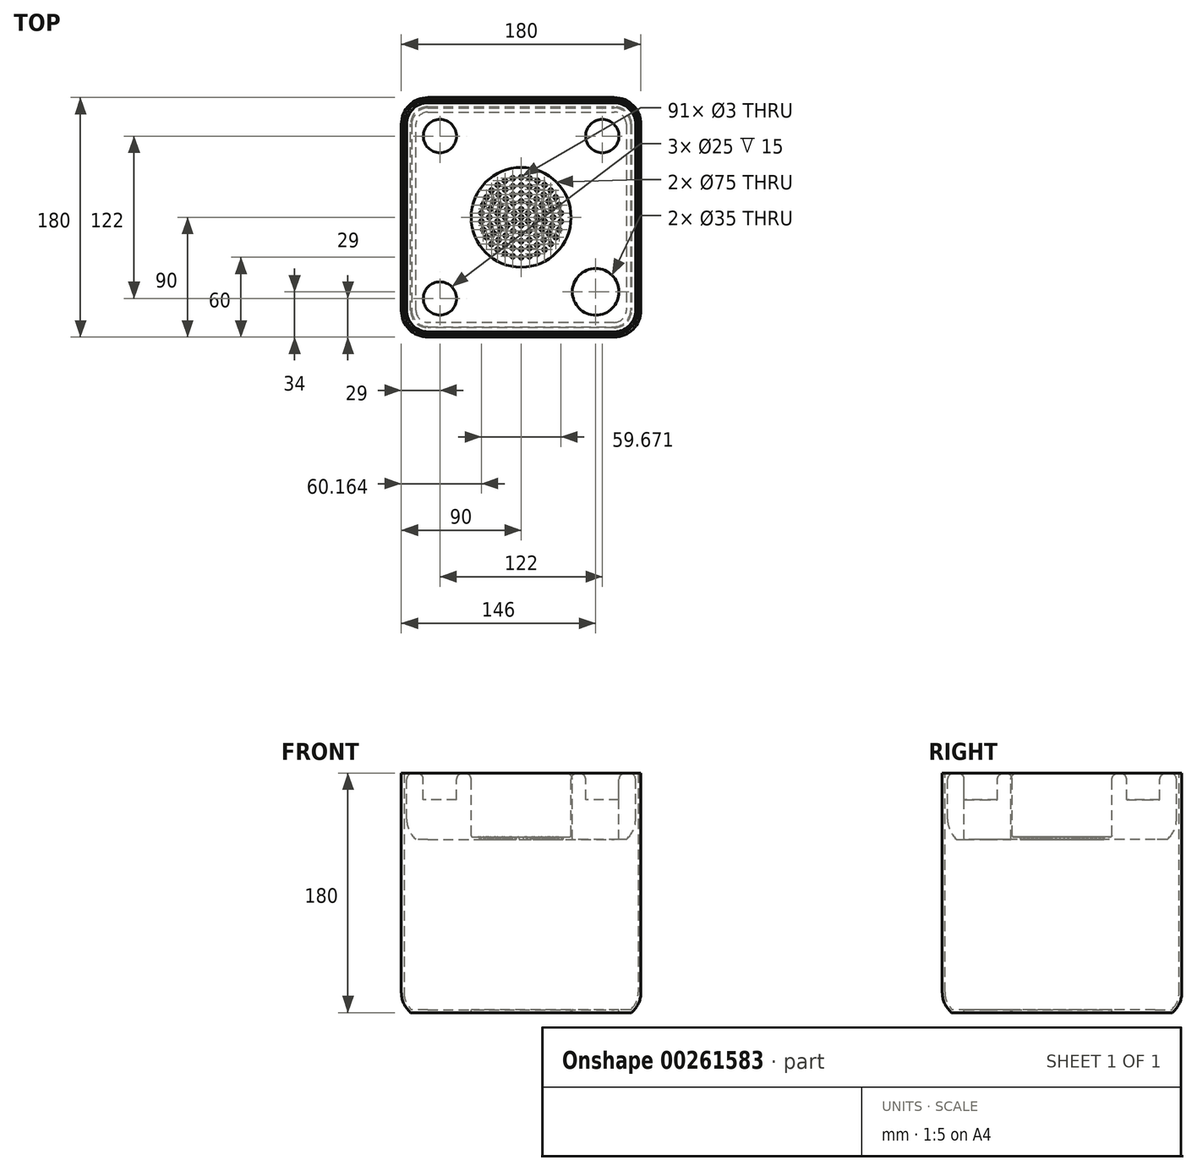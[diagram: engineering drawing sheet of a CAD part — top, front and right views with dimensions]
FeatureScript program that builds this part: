
annotation { "Feature Type Name" : "Feature", "Feature Type Description" : "" }
export const myFeature = defineFeature(function(context is Context, id is Id, definition is map)
    precondition{}
    {
        {
            var Q0;
            Q0=qCreatedBy(makeId("Top.planeOp"),FACE);
            var sketch = newSketch(context, id + "F0", { "sketchPlane" : qUnion([Q0])});
            skLineSegment(sketch, "E0.bottom", {"start": v(-90, 90) * mm, "end": v(90, 90) * mm});
            skLineSegment(sketch, "E0.top", {"start": v(-90, -90) * mm, "end": v(90, -90) * mm});
            skLineSegment(sketch, "E0.left", {"start": v(-90, 90) * mm, "end": v(-90, -90) * mm});
            skLineSegment(sketch, "E0.right", {"start": v(90, 90) * mm, "end": v(90, -90) * mm});
            skPoint(sketch, "E0.middle", {"position": v(0, 0) * mm});
            skSolve(sketch);
        }
        {
            var Q0;
            Q0 = qSketchRegion(id + "F0", true);
            extrude(context, id + "F1", {"entities" : qUnion([Q0]), "depth" : 180 * mm});
        }
        {
            var Q0;
            Q0=makeQuery(id+"F1.opExtrude","SWEPT_EDGE",EDGE,{"disambiguationData":[OSD([sQuery(id+"F0.wireOp",EDGE,"E0.top"),sQuery(id+"F0.wireOp",EDGE,"E0.right")])]});
            var Q1;
            Q1=makeQuery(id+"F1.opExtrude","SWEPT_EDGE",EDGE,{"disambiguationData":[OSD([sQuery(id+"F0.wireOp",EDGE,"E0.top"),sQuery(id+"F0.wireOp",EDGE,"E0.left")])]});
            var Q2;
            Q2=makeQuery(id+"F1.opExtrude","SWEPT_EDGE",EDGE,{"disambiguationData":[OSD([sQuery(id+"F0.wireOp",EDGE,"E0.bottom"),sQuery(id+"F0.wireOp",EDGE,"E0.right")])]});
            var Q3;
            Q3=makeQuery(id+"F1.opExtrude","SWEPT_EDGE",EDGE,{"disambiguationData":[OSD([sQuery(id+"F0.wireOp",EDGE,"E0.bottom"),sQuery(id+"F0.wireOp",EDGE,"E0.left")])]});
            fillet(context, id + "F2", {"entities" : qUnion([Q0, Q1, Q2, Q3]), "radius" : 20 * mm, "tangentPropagation" : true, "allowEdgeOverflow" : false});
        }
        {
            var Q0;
            Q0=makeQuery(id+"F1.opExtrude","CAP_FACE",FACE,{"disambiguationData":[OSD([sQuery(id+"F0.wireOp",EDGE,"E0.bottom"),sQuery(id+"F0.wireOp",EDGE,"E0.top"),sQuery(id+"F0.wireOp",EDGE,"E0.left"),sQuery(id+"F0.wireOp",EDGE,"E0.right")])],"isStart":true});
            chamfer(context, id + "F3", {"entities" : qUnion([Q0]), "width" : 7 * mm, "tangentPropagation" : true});
        }
        {
            var Q0;
            {var subQ0=sQuery(id+"F0.wireOp",EDGE,"E0.left");Q0=makeQuery(id+"F3.opChamfer","BLEND_EDGE",EDGE,{"blendedFrom":[makeQuery(id+"F1.opExtrude","CAP_EDGE",EDGE,{"disambiguationData":[OSD([subQ0])],"isStart":true}),makeQuery(id+"F1.opExtrude","SWEPT_FACE",FACE,{"disambiguationData":[OSD([subQ0])]})],"blendedInto":[makeQuery(id+"F1.opExtrude","SWEPT_FACE",FACE,{"disambiguationData":[OSD([subQ0])]})]});}
            fillet(context, id + "F4", {"entities" : qUnion([Q0]), "radius" : 20 * mm, "tangentPropagation" : true, "allowEdgeOverflow" : false});
        }
        {
            var Q0;
            Q0=makeQuery(id+"F1.opExtrude","CAP_FACE",FACE,{"disambiguationData":[OSD([sQuery(id+"F0.wireOp",EDGE,"E0.bottom"),sQuery(id+"F0.wireOp",EDGE,"E0.top"),sQuery(id+"F0.wireOp",EDGE,"E0.left"),sQuery(id+"F0.wireOp",EDGE,"E0.right")])],"isStart":false});
            shell(context, id + "F5", {"entities" : qUnion([Q0]), "thickness" : 2 * mm});
        }
        {
            var Q0;
            Q0=makeQuery(id+"F4YuCpgrHovAHZC_1.boolean.opBoolean","MERGE",FACE,{"derivedFrom":[makeQuery(id+"F1.opExtrude","CAP_FACE",FACE,{"disambiguationData":[OSD([sQuery(id+"F0.wireOp",EDGE,"E0.bottom"),sQuery(id+"F0.wireOp",EDGE,"E0.top"),sQuery(id+"F0.wireOp",EDGE,"E0.left"),sQuery(id+"F0.wireOp",EDGE,"E0.right")])],"isStart":false}),makeQuery(id+"F4YuCpgrHovAHZC_1.opExtrude","CAP_FACE",FACE,{"disambiguationData":[OSD([sQuery(id+"F18IyqBRE7dcMwR_1.wireOp",EDGE,"iNaZnhlK-WJTm-0Kn5-Of0J-zMqdmAbUonz0.top"),sQuery(id+"F18IyqBRE7dcMwR_1.wireOp",EDGE,"iNaZnhlK-WJTm-0Kn5-Of0J-zMqdmAbUonz0.left"),sQuery(id+"F18IyqBRE7dcMwR_1.wireOp",EDGE,"z2CsC4pT-1LaP-1Rqi-iMAI-N6OsgD8oTBJP"),sQuery(id+"F18IyqBRE7dcMwR_1.wireOp",EDGE,"xvhJzDiT-tZiE-QDcA-WI1C-gXQeY3Zw0ukX"),sQuery(id+"F18IyqBRE7dcMwR_1.wireOp",EDGE,"OlVmHNYn-kKTD-olFf-enFW-YJtCeyeuMl2Y")])],"isStart":true})]});
            var sketch = newSketch(context, id + "F6", { "sketchPlane" : qUnion([Q0])});
            skArc(sketch, "E1.0", {"start": v(-70, 88) * mm, "mid": v(-82.73, 82.73) * mm, "end": v(-88, 70) * mm, "construction": true});
            skLineSegment(sketch, "E1.1", {"start": v(-70, 88) * mm, "end": v(70, 88) * mm, "construction": true});
            skArc(sketch, "E1.2", {"start": v(88, 70) * mm, "mid": v(82.73, 82.73) * mm, "end": v(70, 88) * mm, "construction": true});
            skLineSegment(sketch, "E1.3", {"start": v(88, 70) * mm, "end": v(88, -70) * mm, "construction": true});
            skArc(sketch, "E1.4", {"start": v(70, -88) * mm, "mid": v(82.73, -82.73) * mm, "end": v(88, -70) * mm, "construction": true});
            skLineSegment(sketch, "E1.5", {"start": v(-70, -88) * mm, "end": v(70, -88) * mm, "construction": true});
            skArc(sketch, "E1.6", {"start": v(-88, -70) * mm, "mid": v(-82.73, -82.73) * mm, "end": v(-70, -88) * mm, "construction": true});
            skLineSegment(sketch, "E1.7", {"start": v(-88, 70) * mm, "end": v(-88, -70) * mm, "construction": true});
            skLineSegment(sketch, "E2.0", {"start": v(-70, -86) * mm, "end": v(70, -86) * mm});
            skArc(sketch, "E2.1", {"start": v(-86, -70) * mm, "mid": v(-81.31, -81.31) * mm, "end": v(-70, -86) * mm});
            skArc(sketch, "E2.2", {"start": v(70, -86) * mm, "mid": v(81.31, -81.31) * mm, "end": v(86, -70) * mm});
            skLineSegment(sketch, "E2.3", {"start": v(-86, 70) * mm, "end": v(-86, -70) * mm});
            skLineSegment(sketch, "E2.4", {"start": v(86, 70) * mm, "end": v(86, -70) * mm});
            skArc(sketch, "E2.5", {"start": v(86, 70) * mm, "mid": v(81.31, 81.31) * mm, "end": v(70, 86) * mm});
            skLineSegment(sketch, "E2.6", {"start": v(-70, 86) * mm, "end": v(70, 86) * mm});
            skArc(sketch, "E2.7", {"start": v(-70, 86) * mm, "mid": v(-81.31, 81.31) * mm, "end": v(-86, 70) * mm});
            skSolve(sketch);
        }
        {
            var Q0;
            Q0 = qSketchRegion(id + "F6", true);
            extrude(context, id + "F7", {"entities" : qUnion([Q0]), "oppositeDirection" : true, "depth" : 50 * mm});
        }
        {
            var Q0;
            Q0=makeQuery(id+"F7.opExtrude","CAP_FACE",FACE,{"disambiguationData":[OSD([sQuery(id+"F6.wireOp",EDGE,"E2.7"),sQuery(id+"F6.wireOp",EDGE,"E2.3"),sQuery(id+"F6.wireOp",EDGE,"E2.6"),sQuery(id+"F6.wireOp",EDGE,"E2.1"),sQuery(id+"F6.wireOp",EDGE,"E2.5"),sQuery(id+"F6.wireOp",EDGE,"E2.4"),sQuery(id+"F6.wireOp",EDGE,"E2.2"),sQuery(id+"F6.wireOp",EDGE,"E2.0")])],"isStart":true});
            var sketch = newSketch(context, id + "F8", { "sketchPlane" : qUnion([Q0])});
            skCircle(sketch, "E3", {"center": v(0, 0) * mm, "radius": 37.5 * mm});
            skSolve(sketch);
        }
        {
            var Q0;
            Q0=makeQuery(id+"F8.imprint","IMPRINT",FACE,{"disambiguationData":[TD([[makeQuery(id+"F8.imprint","IMPRINT",EDGE,{"derivedFrom":sQuery(id+"F8.wireOp",EDGE,"E3")}),1.0]])]});
            extrude(context, id + "F9", {"entities" : qUnion([Q0]), "operationType" : NewBodyOperationType.REMOVE, "endBound" : BoundingType.THROUGH_ALL, "oppositeDirection" : true, "depth" : 2 * mm});
        }
        {
            var Q0;
            Q0=makeQuery(id+"F7.opExtrude","CAP_FACE",FACE,{"disambiguationData":[OSD([sQuery(id+"F6.wireOp",EDGE,"E2.7"),sQuery(id+"F6.wireOp",EDGE,"E2.3"),sQuery(id+"F6.wireOp",EDGE,"E2.6"),sQuery(id+"F6.wireOp",EDGE,"E2.1"),sQuery(id+"F6.wireOp",EDGE,"E2.5"),sQuery(id+"F6.wireOp",EDGE,"E2.4"),sQuery(id+"F6.wireOp",EDGE,"E2.2"),sQuery(id+"F6.wireOp",EDGE,"E2.0")])],"isStart":false});
            var sketch = newSketch(context, id + "F10", { "sketchPlane" : qUnion([Q0])});
            skCircle(sketch, "E4.0", {"center": v(0, 0) * mm, "radius": 37.5 * mm});
            skCircle(sketch, "E5", {"center": v(0, 0) * mm, "radius": 6 * mm, "construction": true});
            skCircle(sketch, "E6", {"center": v(0, 0) * mm, "radius": 12 * mm, "construction": true});
            skCircle(sketch, "E7", {"center": v(0, 0) * mm, "radius": 18 * mm, "construction": true});
            skCircle(sketch, "E8", {"center": v(0, 0) * mm, "radius": 24 * mm, "construction": true});
            skCircle(sketch, "E9", {"center": v(0, 0) * mm, "radius": 30 * mm, "construction": true});
            skCircle(sketch, "E10", {"center": v(0, 0) * mm, "radius": 1.5 * mm});
            skCircle(sketch, "E11", {"center": v(0, 6) * mm, "radius": 1.5 * mm});
            skCircle(sketch, "E12", {"center": v(0, 12) * mm, "radius": 1.5 * mm});
            skCircle(sketch, "E13", {"center": v(0, 18) * mm, "radius": 1.5 * mm});
            skCircle(sketch, "E14", {"center": v(0, 24) * mm, "radius": 1.5 * mm});
            skCircle(sketch, "E15", {"center": v(0, 30) * mm, "radius": 1.5 * mm});
            skCircle(sketch, "E16.1.0", {"center": v(-5.2, 3) * mm, "radius": 1.5 * mm});
            skCircle(sketch, "E16.2.0", {"center": v(-5.2, -3) * mm, "radius": 1.5 * mm});
            skCircle(sketch, "E16.3.0", {"center": v(0, -6) * mm, "radius": 1.5 * mm});
            skCircle(sketch, "E16.4.0", {"center": v(5.2, -3) * mm, "radius": 1.5 * mm});
            skCircle(sketch, "E16.5.0", {"center": v(5.2, 3) * mm, "radius": 1.5 * mm});
            skCircle(sketch, "E17.1.0", {"center": v(-6, 10.4) * mm, "radius": 1.5 * mm});
            skCircle(sketch, "E17.2.0", {"center": v(-10.4, 6) * mm, "radius": 1.5 * mm});
            skCircle(sketch, "E17.3.0", {"center": v(-12, 0) * mm, "radius": 1.5 * mm});
            skCircle(sketch, "E17.4.0", {"center": v(-10.4, -6) * mm, "radius": 1.5 * mm});
            skCircle(sketch, "E17.5.0", {"center": v(-6, -10.4) * mm, "radius": 1.5 * mm});
            skCircle(sketch, "E17.6.0", {"center": v(0, -12) * mm, "radius": 1.5 * mm});
            skCircle(sketch, "E17.7.0", {"center": v(6, -10.4) * mm, "radius": 1.5 * mm});
            skCircle(sketch, "E17.8.0", {"center": v(10.4, -6) * mm, "radius": 1.5 * mm});
            skCircle(sketch, "E17.9.0", {"center": v(12, 0) * mm, "radius": 1.5 * mm});
            skCircle(sketch, "E17.10.0", {"center": v(10.4, 6) * mm, "radius": 1.5 * mm});
            skCircle(sketch, "E17.11.0", {"center": v(6, 10.4) * mm, "radius": 1.5 * mm});
            skCircle(sketch, "E18.1.0", {"center": v(-6.16, 16.91) * mm, "radius": 1.5 * mm});
            skCircle(sketch, "E18.2.0", {"center": v(-11.57, 13.79) * mm, "radius": 1.5 * mm});
            skCircle(sketch, "E18.3.0", {"center": v(-15.59, 9) * mm, "radius": 1.5 * mm});
            skCircle(sketch, "E18.4.0", {"center": v(-17.73, 3.13) * mm, "radius": 1.5 * mm});
            skCircle(sketch, "E18.5.0", {"center": v(-17.73, -3.13) * mm, "radius": 1.5 * mm});
            skCircle(sketch, "E18.6.0", {"center": v(-15.59, -9) * mm, "radius": 1.5 * mm});
            skCircle(sketch, "E18.7.0", {"center": v(-11.57, -13.79) * mm, "radius": 1.5 * mm});
            skCircle(sketch, "E18.8.0", {"center": v(-6.16, -16.91) * mm, "radius": 1.5 * mm});
            skCircle(sketch, "E18.9.0", {"center": v(0, -18) * mm, "radius": 1.5 * mm});
            skCircle(sketch, "E18.10.0", {"center": v(6.16, -16.91) * mm, "radius": 1.5 * mm});
            skCircle(sketch, "E18.11.0", {"center": v(11.57, -13.79) * mm, "radius": 1.5 * mm});
            skCircle(sketch, "E18.12.0", {"center": v(15.59, -9) * mm, "radius": 1.5 * mm});
            skCircle(sketch, "E18.13.0", {"center": v(17.73, -3.13) * mm, "radius": 1.5 * mm});
            skCircle(sketch, "E18.14.0", {"center": v(17.73, 3.13) * mm, "radius": 1.5 * mm});
            skCircle(sketch, "E18.15.0", {"center": v(15.59, 9) * mm, "radius": 1.5 * mm});
            skCircle(sketch, "E18.16.0", {"center": v(11.57, 13.79) * mm, "radius": 1.5 * mm});
            skCircle(sketch, "E18.17.0", {"center": v(6.16, 16.91) * mm, "radius": 1.5 * mm});
            skCircle(sketch, "E19.1.0", {"center": v(-6.21, 23.18) * mm, "radius": 1.5 * mm});
            skCircle(sketch, "E19.2.0", {"center": v(-12, 20.78) * mm, "radius": 1.5 * mm});
            skCircle(sketch, "E19.3.0", {"center": v(-16.97, 16.97) * mm, "radius": 1.5 * mm});
            skCircle(sketch, "E19.4.0", {"center": v(-20.78, 12) * mm, "radius": 1.5 * mm});
            skCircle(sketch, "E19.5.0", {"center": v(-23.18, 6.21) * mm, "radius": 1.5 * mm});
            skCircle(sketch, "E19.6.0", {"center": v(-24, 0) * mm, "radius": 1.5 * mm});
            skCircle(sketch, "E19.7.0", {"center": v(-23.18, -6.21) * mm, "radius": 1.5 * mm});
            skCircle(sketch, "E19.8.0", {"center": v(-20.78, -12) * mm, "radius": 1.5 * mm});
            skCircle(sketch, "E19.9.0", {"center": v(-16.97, -16.97) * mm, "radius": 1.5 * mm});
            skCircle(sketch, "E19.10.0", {"center": v(-12, -20.78) * mm, "radius": 1.5 * mm});
            skCircle(sketch, "E19.11.0", {"center": v(-6.21, -23.18) * mm, "radius": 1.5 * mm});
            skCircle(sketch, "E19.12.0", {"center": v(0, -24) * mm, "radius": 1.5 * mm});
            skCircle(sketch, "E19.13.0", {"center": v(6.21, -23.18) * mm, "radius": 1.5 * mm});
            skCircle(sketch, "E19.14.0", {"center": v(12, -20.78) * mm, "radius": 1.5 * mm});
            skCircle(sketch, "E19.15.0", {"center": v(16.97, -16.97) * mm, "radius": 1.5 * mm});
            skCircle(sketch, "E19.16.0", {"center": v(20.78, -12) * mm, "radius": 1.5 * mm});
            skCircle(sketch, "E19.17.0", {"center": v(23.18, -6.21) * mm, "radius": 1.5 * mm});
            skCircle(sketch, "E19.18.0", {"center": v(24, 0) * mm, "radius": 1.5 * mm});
            skCircle(sketch, "E19.19.0", {"center": v(23.18, 6.21) * mm, "radius": 1.5 * mm});
            skCircle(sketch, "E19.20.0", {"center": v(20.78, 12) * mm, "radius": 1.5 * mm});
            skCircle(sketch, "E19.21.0", {"center": v(16.97, 16.97) * mm, "radius": 1.5 * mm});
            skCircle(sketch, "E19.22.0", {"center": v(12, 20.78) * mm, "radius": 1.5 * mm});
            skCircle(sketch, "E19.23.0", {"center": v(6.21, 23.18) * mm, "radius": 1.5 * mm});
            skCircle(sketch, "E20.1.0", {"center": v(-6.24, 29.34) * mm, "radius": 1.5 * mm});
            skCircle(sketch, "E20.2.0", {"center": v(-12.2, 27.4) * mm, "radius": 1.5 * mm});
            skCircle(sketch, "E20.3.0", {"center": v(-17.63, 24.27) * mm, "radius": 1.5 * mm});
            skCircle(sketch, "E20.4.0", {"center": v(-22.3, 20.07) * mm, "radius": 1.5 * mm});
            skCircle(sketch, "E20.5.0", {"center": v(-25.98, 15) * mm, "radius": 1.5 * mm});
            skCircle(sketch, "E20.6.0", {"center": v(-28.53, 9.27) * mm, "radius": 1.5 * mm});
            skCircle(sketch, "E20.7.0", {"center": v(-29.84, 3.14) * mm, "radius": 1.5 * mm});
            skCircle(sketch, "E20.8.0", {"center": v(-29.84, -3.14) * mm, "radius": 1.5 * mm});
            skCircle(sketch, "E20.9.0", {"center": v(-28.53, -9.27) * mm, "radius": 1.5 * mm});
            skCircle(sketch, "E20.10.0", {"center": v(-25.98, -15) * mm, "radius": 1.5 * mm});
            skCircle(sketch, "E20.11.0", {"center": v(-22.3, -20.07) * mm, "radius": 1.5 * mm});
            skCircle(sketch, "E20.12.0", {"center": v(-17.63, -24.27) * mm, "radius": 1.5 * mm});
            skCircle(sketch, "E20.13.0", {"center": v(-12.2, -27.4) * mm, "radius": 1.5 * mm});
            skCircle(sketch, "E20.14.0", {"center": v(-6.24, -29.34) * mm, "radius": 1.5 * mm});
            skCircle(sketch, "E20.15.0", {"center": v(0, -30) * mm, "radius": 1.5 * mm});
            skCircle(sketch, "E20.16.0", {"center": v(6.24, -29.34) * mm, "radius": 1.5 * mm});
            skCircle(sketch, "E20.17.0", {"center": v(12.2, -27.4) * mm, "radius": 1.5 * mm});
            skCircle(sketch, "E20.18.0", {"center": v(17.63, -24.27) * mm, "radius": 1.5 * mm});
            skCircle(sketch, "E20.19.0", {"center": v(22.3, -20.07) * mm, "radius": 1.5 * mm});
            skCircle(sketch, "E20.20.0", {"center": v(25.98, -15) * mm, "radius": 1.5 * mm});
            skCircle(sketch, "E20.21.0", {"center": v(28.53, -9.27) * mm, "radius": 1.5 * mm});
            skCircle(sketch, "E20.22.0", {"center": v(29.84, -3.14) * mm, "radius": 1.5 * mm});
            skCircle(sketch, "E20.23.0", {"center": v(29.84, 3.14) * mm, "radius": 1.5 * mm});
            skCircle(sketch, "E20.24.0", {"center": v(28.53, 9.27) * mm, "radius": 1.5 * mm});
            skCircle(sketch, "E20.25.0", {"center": v(25.98, 15) * mm, "radius": 1.5 * mm});
            skCircle(sketch, "E20.26.0", {"center": v(22.3, 20.07) * mm, "radius": 1.5 * mm});
            skCircle(sketch, "E20.27.0", {"center": v(17.63, 24.27) * mm, "radius": 1.5 * mm});
            skCircle(sketch, "E20.28.0", {"center": v(12.2, 27.4) * mm, "radius": 1.5 * mm});
            skCircle(sketch, "E20.29.0", {"center": v(6.24, 29.34) * mm, "radius": 1.5 * mm});
            skSolve(sketch);
        }
        {
            var Q0;
            Q0 = qSketchRegion(id + "F10", true);
            extrude(context, id + "F11", {"entities" : qUnion([Q0]), "operationType" : NewBodyOperationType.ADD, "oppositeDirection" : true, "depth" : 2 * mm});
        }
        {
            var Q0;
            Q0=makeQuery(id+"F7.opExtrude","CAP_FACE",FACE,{"disambiguationData":[OSD([sQuery(id+"F6.wireOp",EDGE,"E2.7"),sQuery(id+"F6.wireOp",EDGE,"E2.3"),sQuery(id+"F6.wireOp",EDGE,"E2.6"),sQuery(id+"F6.wireOp",EDGE,"E2.1"),sQuery(id+"F6.wireOp",EDGE,"E2.5"),sQuery(id+"F6.wireOp",EDGE,"E2.4"),sQuery(id+"F6.wireOp",EDGE,"E2.2"),sQuery(id+"F6.wireOp",EDGE,"E2.0")])],"isStart":true});
            var sketch = newSketch(context, id + "F12", { "sketchPlane" : qUnion([Q0])});
            skCircle(sketch, "E21", {"center": v(-61, -61) * mm, "radius": 12.5 * mm});
            skCircle(sketch, "E22", {"center": v(-61, 61) * mm, "radius": 12.5 * mm});
            skCircle(sketch, "E23", {"center": v(61, 61) * mm, "radius": 12.5 * mm});
            skSolve(sketch);
        }
        {
            var Q0;
            Q0 = qSketchRegion(id + "F12", true);
            extrude(context, id + "F13", {"entities" : qUnion([Q0]), "operationType" : NewBodyOperationType.REMOVE, "oppositeDirection" : true, "depth" : 20 * mm});
        }
        {
            var Q0;
            Q0=makeQuery(id+"F7.opExtrude","CAP_FACE",FACE,{"disambiguationData":[OSD([sQuery(id+"F6.wireOp",EDGE,"E2.7"),sQuery(id+"F6.wireOp",EDGE,"E2.3"),sQuery(id+"F6.wireOp",EDGE,"E2.6"),sQuery(id+"F6.wireOp",EDGE,"E2.1"),sQuery(id+"F6.wireOp",EDGE,"E2.5"),sQuery(id+"F6.wireOp",EDGE,"E2.4"),sQuery(id+"F6.wireOp",EDGE,"E2.2"),sQuery(id+"F6.wireOp",EDGE,"E2.0")])],"isStart":true});
            var sketch = newSketch(context, id + "F14", { "sketchPlane" : qUnion([Q0])});
            skCircle(sketch, "E24", {"center": v(56, -56) * mm, "radius": 17.5 * mm});
            skSolve(sketch);
        }
        {
            var Q0;
            Q0 = qSketchRegion(id + "F14", true);
            extrude(context, id + "F15", {"entities" : qUnion([Q0]), "operationType" : NewBodyOperationType.REMOVE, "endBound" : BoundingType.THROUGH_ALL, "oppositeDirection" : true, "depth" : 25 * mm});
        }
        {
            var Q0;
            Q0=makeQuery(id+"F7.opExtrude","CAP_FACE",FACE,{"disambiguationData":[OSD([sQuery(id+"F6.wireOp",EDGE,"E2.7"),sQuery(id+"F6.wireOp",EDGE,"E2.3"),sQuery(id+"F6.wireOp",EDGE,"E2.6"),sQuery(id+"F6.wireOp",EDGE,"E2.1"),sQuery(id+"F6.wireOp",EDGE,"E2.5"),sQuery(id+"F6.wireOp",EDGE,"E2.4"),sQuery(id+"F6.wireOp",EDGE,"E2.2"),sQuery(id+"F6.wireOp",EDGE,"E2.0")])],"isStart":true});
            var Q1;
            Q1=makeQuery(id+"F11.opExtrude","CAP_EDGE",EDGE,{"disambiguationData":[OSD([sQuery(id+"F10.wireOp",EDGE,"E4.0")])],"isStart":false});
            fillet(context, id + "F16", {"entities" : qUnion([Q0, Q1]), "radius" : 5 * mm, "tangentPropagation" : true, "allowEdgeOverflow" : false});
        }
        {
            var Q0;
            Q0=makeQuery(id+"F11.opExtrude","CAP_FACE",FACE,{"disambiguationData":[OSD([sQuery(id+"F10.wireOp",EDGE,"E4.0"),sQuery(id+"F10.wireOp",EDGE,"E10"),sQuery(id+"F10.wireOp",EDGE,"E11"),sQuery(id+"F10.wireOp",EDGE,"E12"),sQuery(id+"F10.wireOp",EDGE,"E13"),sQuery(id+"F10.wireOp",EDGE,"E14"),sQuery(id+"F10.wireOp",EDGE,"E15"),sQuery(id+"F10.wireOp",EDGE,"E16.1.0"),sQuery(id+"F10.wireOp",EDGE,"E16.2.0"),sQuery(id+"F10.wireOp",EDGE,"E16.3.0"),sQuery(id+"F10.wireOp",EDGE,"E16.4.0"),sQuery(id+"F10.wireOp",EDGE,"E16.5.0"),sQuery(id+"F10.wireOp",EDGE,"E17.1.0"),sQuery(id+"F10.wireOp",EDGE,"E17.2.0"),sQuery(id+"F10.wireOp",EDGE,"E17.3.0"),sQuery(id+"F10.wireOp",EDGE,"E17.4.0"),sQuery(id+"F10.wireOp",EDGE,"E17.5.0"),sQuery(id+"F10.wireOp",EDGE,"E17.6.0"),sQuery(id+"F10.wireOp",EDGE,"E17.7.0"),sQuery(id+"F10.wireOp",EDGE,"E17.8.0"),sQuery(id+"F10.wireOp",EDGE,"E17.9.0"),sQuery(id+"F10.wireOp",EDGE,"E17.10.0"),sQuery(id+"F10.wireOp",EDGE,"E17.11.0"),sQuery(id+"F10.wireOp",EDGE,"E18.1.0"),sQuery(id+"F10.wireOp",EDGE,"E18.2.0"),sQuery(id+"F10.wireOp",EDGE,"E18.3.0"),sQuery(id+"F10.wireOp",EDGE,"E18.4.0"),sQuery(id+"F10.wireOp",EDGE,"E18.5.0"),sQuery(id+"F10.wireOp",EDGE,"E18.6.0"),sQuery(id+"F10.wireOp",EDGE,"E18.7.0"),sQuery(id+"F10.wireOp",EDGE,"E18.8.0"),sQuery(id+"F10.wireOp",EDGE,"E18.9.0"),sQuery(id+"F10.wireOp",EDGE,"E18.10.0"),sQuery(id+"F10.wireOp",EDGE,"E18.11.0"),sQuery(id+"F10.wireOp",EDGE,"E18.12.0"),sQuery(id+"F10.wireOp",EDGE,"E18.13.0"),sQuery(id+"F10.wireOp",EDGE,"E18.14.0"),sQuery(id+"F10.wireOp",EDGE,"E18.15.0"),sQuery(id+"F10.wireOp",EDGE,"E18.16.0"),sQuery(id+"F10.wireOp",EDGE,"E18.17.0"),sQuery(id+"F10.wireOp",EDGE,"E19.1.0"),sQuery(id+"F10.wireOp",EDGE,"E19.2.0"),sQuery(id+"F10.wireOp",EDGE,"E19.3.0"),sQuery(id+"F10.wireOp",EDGE,"E19.4.0"),sQuery(id+"F10.wireOp",EDGE,"E19.5.0"),sQuery(id+"F10.wireOp",EDGE,"E19.6.0"),sQuery(id+"F10.wireOp",EDGE,"E19.7.0"),sQuery(id+"F10.wireOp",EDGE,"E19.8.0"),sQuery(id+"F10.wireOp",EDGE,"E19.9.0"),sQuery(id+"F10.wireOp",EDGE,"E19.10.0"),sQuery(id+"F10.wireOp",EDGE,"E19.11.0"),sQuery(id+"F10.wireOp",EDGE,"E19.12.0"),sQuery(id+"F10.wireOp",EDGE,"E19.13.0"),sQuery(id+"F10.wireOp",EDGE,"E19.14.0"),sQuery(id+"F10.wireOp",EDGE,"E19.15.0"),sQuery(id+"F10.wireOp",EDGE,"E19.16.0"),sQuery(id+"F10.wireOp",EDGE,"E19.17.0"),sQuery(id+"F10.wireOp",EDGE,"E19.18.0"),sQuery(id+"F10.wireOp",EDGE,"E19.19.0"),sQuery(id+"F10.wireOp",EDGE,"E19.20.0"),sQuery(id+"F10.wireOp",EDGE,"E19.21.0"),sQuery(id+"F10.wireOp",EDGE,"E19.22.0"),sQuery(id+"F10.wireOp",EDGE,"E19.23.0"),sQuery(id+"F10.wireOp",EDGE,"E20.1.0"),sQuery(id+"F10.wireOp",EDGE,"E20.2.0"),sQuery(id+"F10.wireOp",EDGE,"E20.3.0"),sQuery(id+"F10.wireOp",EDGE,"E20.4.0"),sQuery(id+"F10.wireOp",EDGE,"E20.5.0"),sQuery(id+"F10.wireOp",EDGE,"E20.6.0"),sQuery(id+"F10.wireOp",EDGE,"E20.7.0"),sQuery(id+"F10.wireOp",EDGE,"E20.8.0"),sQuery(id+"F10.wireOp",EDGE,"E20.9.0"),sQuery(id+"F10.wireOp",EDGE,"E20.10.0"),sQuery(id+"F10.wireOp",EDGE,"E20.11.0"),sQuery(id+"F10.wireOp",EDGE,"E20.12.0"),sQuery(id+"F10.wireOp",EDGE,"E20.13.0"),sQuery(id+"F10.wireOp",EDGE,"E20.14.0"),sQuery(id+"F10.wireOp",EDGE,"E20.15.0"),sQuery(id+"F10.wireOp",EDGE,"E20.16.0"),sQuery(id+"F10.wireOp",EDGE,"E20.17.0"),sQuery(id+"F10.wireOp",EDGE,"E20.18.0"),sQuery(id+"F10.wireOp",EDGE,"E20.19.0"),sQuery(id+"F10.wireOp",EDGE,"E20.20.0"),sQuery(id+"F10.wireOp",EDGE,"E20.21.0"),sQuery(id+"F10.wireOp",EDGE,"E20.22.0"),sQuery(id+"F10.wireOp",EDGE,"E20.23.0"),sQuery(id+"F10.wireOp",EDGE,"E20.24.0"),sQuery(id+"F10.wireOp",EDGE,"E20.25.0"),sQuery(id+"F10.wireOp",EDGE,"E20.26.0"),sQuery(id+"F10.wireOp",EDGE,"E20.27.0"),sQuery(id+"F10.wireOp",EDGE,"E20.28.0"),sQuery(id+"F10.wireOp",EDGE,"E20.29.0")])],"isStart":false});
            fillet(context, id + "F17", {"entities" : qUnion([Q0]), "radius" : 1 * mm, "tangentPropagation" : true, "allowEdgeOverflow" : false});
        }
        {
            var Q0;
            Q0=makeQuery(id+"F7.opExtrude","CAP_EDGE",EDGE,{"disambiguationData":[OSD([sQuery(id+"F6.wireOp",EDGE,"E2.0")])],"isStart":false});
            chamfer(context, id + "F18", {"entities" : qUnion([Q0]), "width" : 7 * mm, "tangentPropagation" : true});
        }
        {
            var Q0;
            {var subQ0=sQuery(id+"F6.wireOp",EDGE,"E2.0");Q0=makeQuery(id+"F18.opChamfer","BLEND_EDGE",EDGE,{"blendedFrom":[makeQuery(id+"F7.opExtrude","CAP_EDGE",EDGE,{"disambiguationData":[OSD([subQ0])],"isStart":false}),makeQuery(id+"F7.opExtrude","SWEPT_FACE",FACE,{"disambiguationData":[OSD([subQ0])]})],"blendedInto":[makeQuery(id+"F7.opExtrude","SWEPT_FACE",FACE,{"disambiguationData":[OSD([subQ0])]})]});}
            fillet(context, id + "F19", {"entities" : qUnion([Q0]), "radius" : 20 * mm, "tangentPropagation" : true, "allowEdgeOverflow" : false});
        }
    });
